# Revit family: Контроллер замковый PERCo_CL15.3, CL15.7
name_source: partatom
category: Охранная сигнализация
units: mm (PartAtom-declared; Revit-internal decimal feet)

## family parameters
Общий = Нет
Основа = Грань
При загрузке вырезать с полостями = Нет
Размер круглого соединителя = Использовать диаметр
Сохранять ориентацию аннотаций = Да
Тип детали = Нормальный
Точка расчета площади = Нет

## types (2) — shared parameters
ADSK_Единица измерения = шт.
ADSK_Завод-изготовитель = PERCo
ADSK_Количество = 1
ADSK_Масса_Текст = не более 0,15 кг
ADSK_Материал наименование = Корпус выполнен из ударопрочного АБС-пластика
ADSK_Напряжение = 12 В
ADSK_Номинальная мощность = 2 В·А
ADSK_Ток = 0 А
Габаритные размеры = 150×50×20 мм
Кол-во выносных считывателей = Не предусмотрено
Кол-во контроллеров 2-го уровня = Не предусмотрено
Кол-во подключаемых замков = 1
Кол-во подключаемых турникетов = 1 (одно направление)
Кол-во пользователей = до 50 000
Кол-во событий = до 150 000
Наличие встроенного считывателя = Да
Наличие сканера отпечатка пальцев = Нет
Отметка по умолчанию = 1500 мм
Подключение к электросети = 220В
Степень защиты оболочки = IP54
Температура использования = от +1°С до +45°С
Тип интерфейса = Ethernet

## per-type parameters (varying)
| type | ADSK_Наименование | ADSK_Наименование краткое | Формат читаемых карт |
| CL15.3 | Контроллер замка PERCo-CL15.3 со встроенным считывателем для карт формата EMM и HID | Контроллер CL15.3 | EMM, HID Prox |
| CL15.7 | Контроллер замка PERCo-CL15.7 со встроенным считывателем для карт формата Mifare | Контроллер CL15.7 | Mifare |
